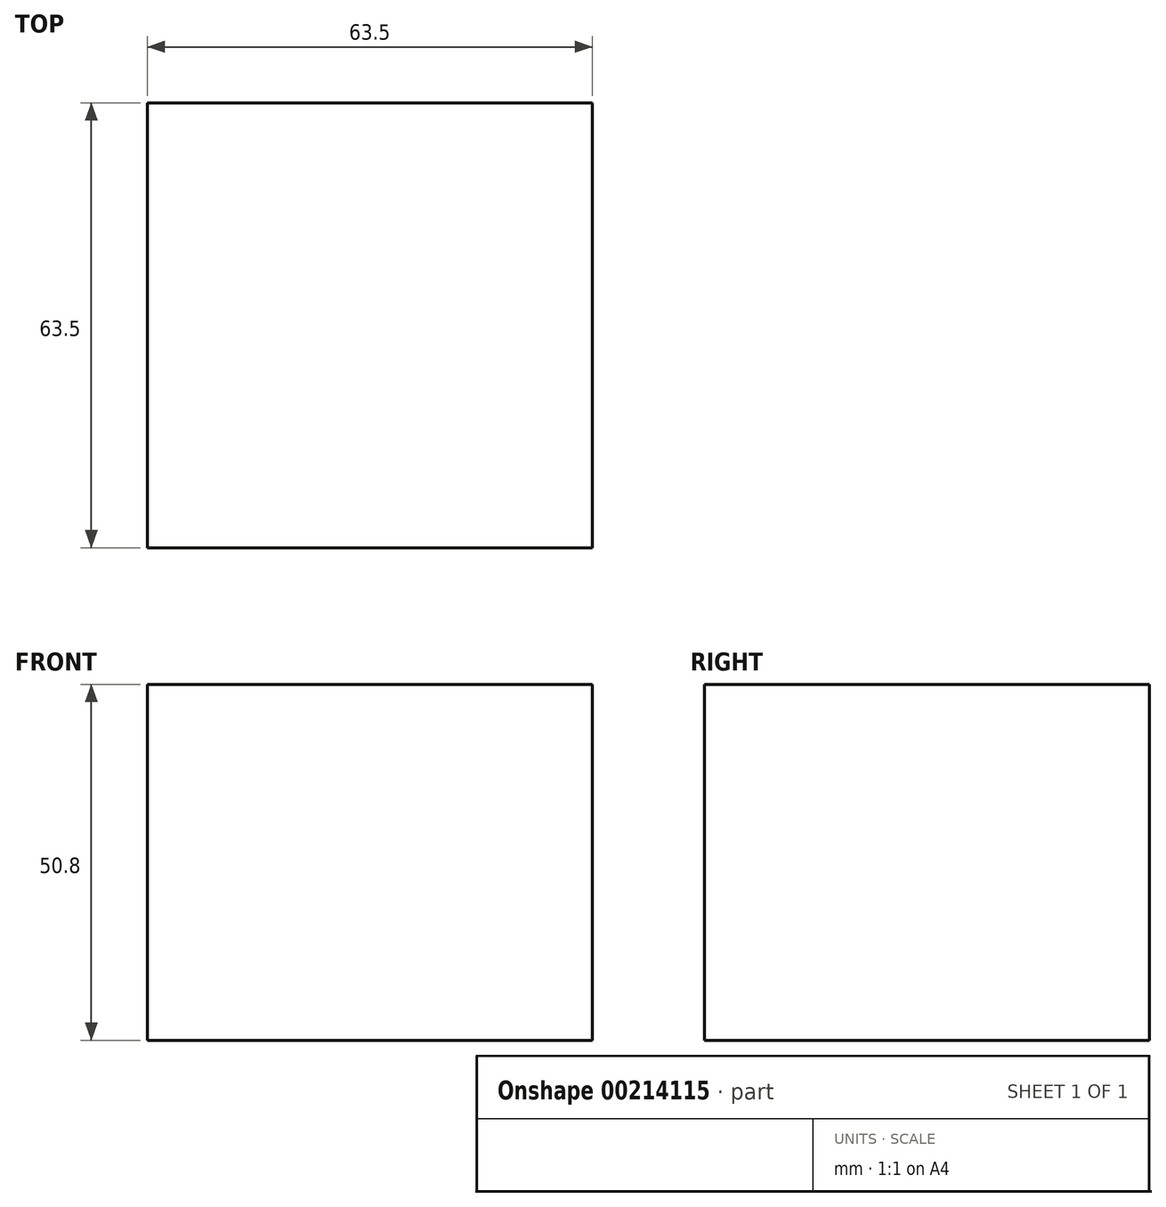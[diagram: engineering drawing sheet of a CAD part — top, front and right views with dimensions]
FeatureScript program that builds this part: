
annotation { "Feature Type Name" : "Feature", "Feature Type Description" : "" }
export const myFeature = defineFeature(function(context is Context, id is Id, definition is map)
    precondition{}
    {
        {
            var Q0;
            Q0=qCreatedBy(makeId("Top.planeOp"),FACE);
            var sketch = newSketch(context, id + "F0", { "sketchPlane" : qUnion([Q0])});
            skLineSegment(sketch, "E0.bottom", {"start": v(0, 0) * mm, "end": v(63.5, 0) * mm});
            skLineSegment(sketch, "E0.top", {"start": v(0, 63.5) * mm, "end": v(63.5, 63.5) * mm});
            skLineSegment(sketch, "E0.left", {"start": v(0, 0) * mm, "end": v(0, 63.5) * mm});
            skLineSegment(sketch, "E0.right", {"start": v(63.5, 0) * mm, "end": v(63.5, 63.5) * mm});
            skSolve(sketch);
        }
        {
            var Q0;
            Q0=makeQuery(id+"F0.imprint","IMPRINT",FACE,{"disambiguationData":[TD([[makeQuery(id+"F0.imprint","IMPRINT",EDGE,{"derivedFrom":sQuery(id+"F0.wireOp",EDGE,"E0.bottom")}),1.0]])]});
            extrude(context, id + "F1", {"entities" : qUnion([Q0]), "depth" : 50.8 * mm});
        }
    });
